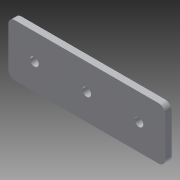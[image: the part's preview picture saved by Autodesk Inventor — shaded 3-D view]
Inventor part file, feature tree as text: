
AUTODESK INVENTOR PART (.ipt)
format: ipt  version: 2014 (Build 180170000, 170)  size: 89,600 bytes
history: native  units: in
note: dims shown in document units (in); Inventor stores cm internally (conversion verified against a paired STEP export)
features: extrude x1, fillet x1, sketch x1
ambient origin geometry x8: Origin, YZ Plane, XZ Plane, XY Plane, X Axis, Y Axis, Z Axis, Center Point
bodies: Solid1 (feature_tree)
feature tree (3):
  extrude  "Extrusion1"  Depth=1.0in
  fillet  "Fillet1"  Radius=0.164in
  sketch  "Sketch1"  dims[d0=3.0in d1=1.0in d2=0.164in d3=0.5in d4=0.5in d5=1.1811in d7=1.0in d8=0.3937in d10=1.0in d12=0.125in d13=0.0in d14=0.125in]
